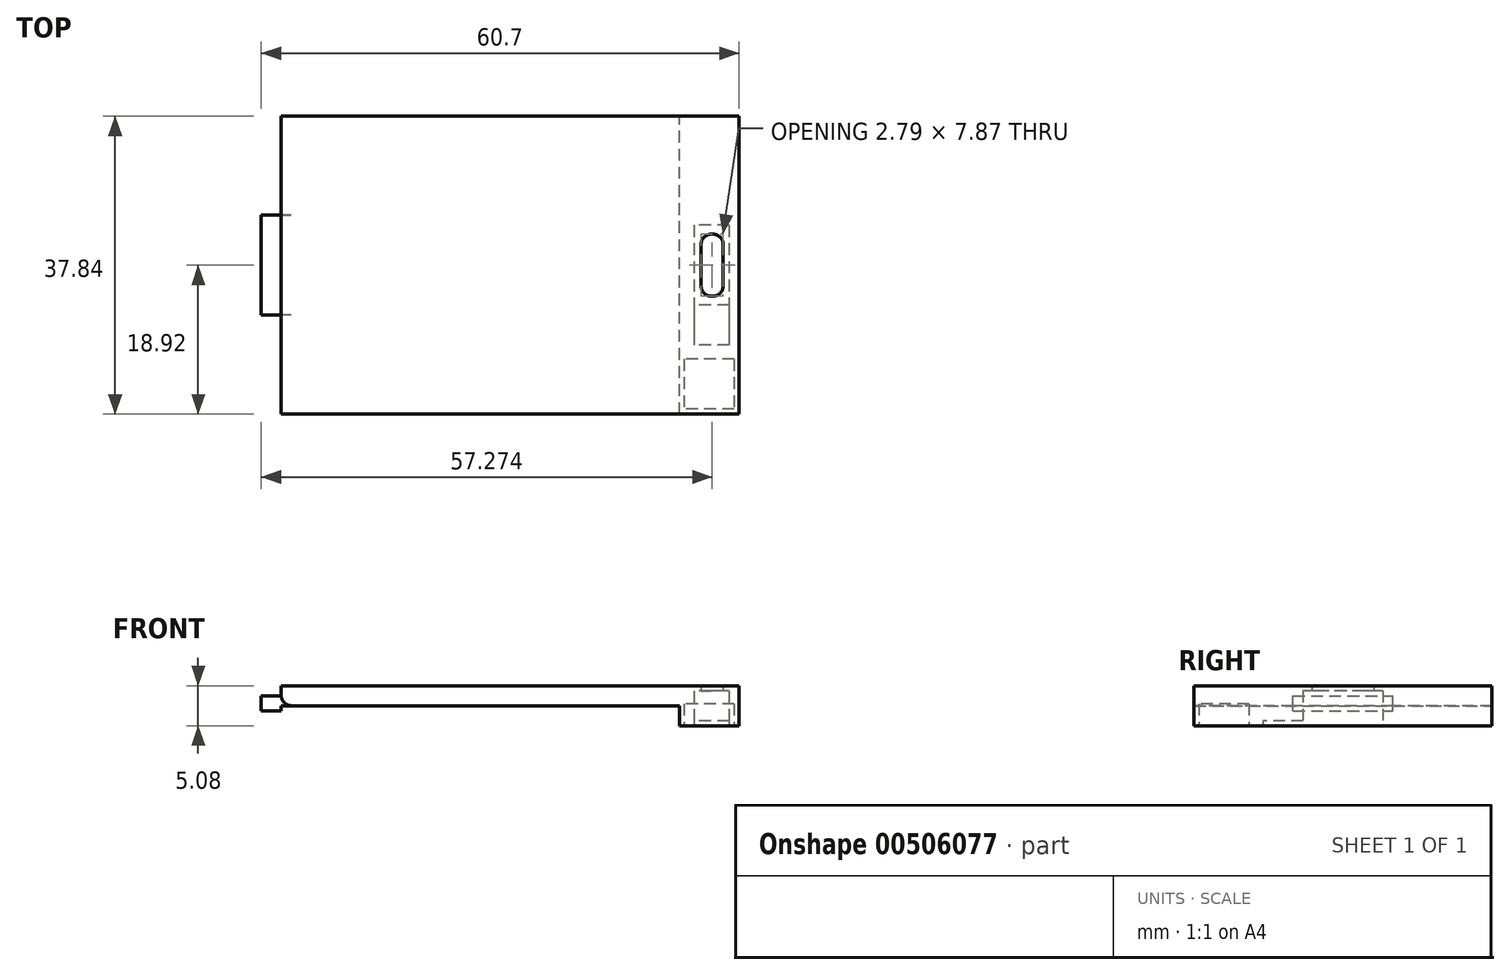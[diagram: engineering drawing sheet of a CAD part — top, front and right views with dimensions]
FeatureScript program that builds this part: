
annotation { "Feature Type Name" : "Feature", "Feature Type Description" : "" }
export const myFeature = defineFeature(function(context is Context, id is Id, definition is map)
    precondition{}
    {
        {
            var Q0;
            Q0=qCreatedBy(makeId("Top.planeOp"),FACE);
            var sketch = newSketch(context, id + "F0", { "sketchPlane" : qUnion([Q0])});
            skLineSegment(sketch, "E0.bottom", {"start": v(29.08, 18.92) * mm, "end": v(-29.08, 18.92) * mm});
            skLineSegment(sketch, "E0.top", {"start": v(29.08, -18.92) * mm, "end": v(-29.08, -18.92) * mm});
            skLineSegment(sketch, "E0.left", {"start": v(29.08, 18.92) * mm, "end": v(29.08, -18.92) * mm});
            skLineSegment(sketch, "E0.right", {"start": v(-29.08, 18.92) * mm, "end": v(-29.08, -18.92) * mm});
            skPoint(sketch, "E0.middle", {"position": v(0, 0) * mm});
            skSolve(sketch);
        }
        {
            var Q0;
            Q0=makeQuery(id+"F0.imprint","IMPRINT",FACE,{"disambiguationData":[TD([[makeQuery(id+"F0.imprint","IMPRINT",EDGE,{"derivedFrom":sQuery(id+"F0.wireOp",EDGE,"E0.bottom")}),1.0]])]});
            extrude(context, id + "F1", {"entities" : qUnion([Q0]), "depth" : 2.54 * mm});
        }
        {
            var Q0;
            Q0=makeQuery(id+"F1.opExtrude","CAP_FACE",FACE,{"disambiguationData":[OSD([sQuery(id+"F0.wireOp",EDGE,"E0.bottom"),sQuery(id+"F0.wireOp",EDGE,"E0.top"),sQuery(id+"F0.wireOp",EDGE,"E0.left"),sQuery(id+"F0.wireOp",EDGE,"E0.right")])],"isStart":true});
            var sketch = newSketch(context, id + "F2", { "sketchPlane" : qUnion([Q0])});
            skLineSegment(sketch, "E1.bottom", {"start": v(29.08, 18.92) * mm, "end": v(21.49, 18.92) * mm});
            skLineSegment(sketch, "E1.top", {"start": v(29.08, -18.92) * mm, "end": v(21.49, -18.92) * mm});
            skLineSegment(sketch, "E1.left", {"start": v(29.08, 18.92) * mm, "end": v(29.08, -18.92) * mm});
            skLineSegment(sketch, "E1.right", {"start": v(21.49, 18.92) * mm, "end": v(21.49, -18.92) * mm});
            skSolve(sketch);
        }
        {
            var Q0;
            Q0=makeQuery(id+"F2.imprint","IMPRINT",FACE,{"disambiguationData":[TD([[makeQuery(id+"F2.imprint","IMPRINT",EDGE,{"derivedFrom":sQuery(id+"F2.wireOp",EDGE,"E1.bottom")}),1.0]])]});
            extrude(context, id + "F3", {"entities" : qUnion([Q0]), "operationType" : NewBodyOperationType.ADD, "depth" : 2.54 * mm});
        }
        {
            var Q0;
            Q0=makeQuery(id+"F1.opExtrude","SWEPT_FACE",FACE,{"disambiguationData":[OSD([sQuery(id+"F0.wireOp",EDGE,"E0.right")])]});
            var sketch = newSketch(context, id + "F4", { "sketchPlane" : qUnion([Q0])});
            skLineSegment(sketch, "E2.bottom", {"start": v(6.35, -0.63) * mm, "end": v(-6.35, -0.64) * mm});
            skLineSegment(sketch, "E2.top", {"start": v(6.35, 1.27) * mm, "end": v(-6.35, 1.27) * mm});
            skLineSegment(sketch, "E2.left", {"start": v(6.35, -0.63) * mm, "end": v(6.35, 1.27) * mm});
            skLineSegment(sketch, "E2.right", {"start": v(-6.35, -0.64) * mm, "end": v(-6.35, 1.27) * mm});
            skPoint(sketch, "E2.middle", {"position": v(0, 0.32) * mm});
            skSolve(sketch);
        }
        {
            var Q0;
            {var subQ0=sQuery(id+"F4.wireOp",EDGE,"E2.bottom");Q0=makeQuery(id+"F4.imprint","IMPRINT",FACE,{"disambiguationData":[TD([[makeQuery(id+"F4.imprint","IMPRINT",EDGE,{"derivedFrom":subQ0}),-1.0]])]});}
            var Q1;
            {var subQ0=sQuery(id+"F4.wireOp",EDGE,"E2.top");Q1=makeQuery(id+"F4.imprint","IMPRINT",FACE,{"disambiguationData":[TD([[makeQuery(id+"F4.imprint","IMPRINT",EDGE,{"derivedFrom":subQ0}),1.0]])]});}
            extrude(context, id + "F5", {"entities" : qUnion([Q0, Q1]), "operationType" : NewBodyOperationType.ADD, "depth" : 2.54 * mm});
        }
        {
            var Q0;
            {var subQ0=sQuery(id+"F0.wireOp",EDGE,"E0.right");Q0=makeQuery(id+"F5.boolean.opBoolean","SPLIT",EDGE,{"disambiguationData":[topologyDisambiguationEdgeConnected([makeQuery(id+"F1.opExtrude","CAP_FACE",FACE,{"disambiguationData":[OSD([sQuery(id+"F0.wireOp",EDGE,"E0.bottom"),sQuery(id+"F0.wireOp",EDGE,"E0.top"),sQuery(id+"F0.wireOp",EDGE,"E0.left"),subQ0])],"isStart":true}),makeQuery(id+"F5.opExtrude","CAP_FACE",FACE,{"disambiguationData":[OSD([sQuery(id+"F4.wireOp",EDGE,"E2.bottom"),sQuery(id+"F4.wireOp",EDGE,"E2.top"),sQuery(id+"F4.wireOp",EDGE,"E2.left"),sQuery(id+"F4.wireOp",EDGE,"E2.right")])],"isStart":true})])],"derivedFrom":makeQuery(id+"F1.opExtrude","CAP_EDGE",EDGE,{"disambiguationData":[OSD([subQ0])],"isStart":true})});}
            fillet(context, id + "F6", {"entities" : qUnion([Q0]), "radius" : 1.27 * mm, "tangentPropagation" : true, "allowEdgeOverflow" : false});
        }
        {
            var Q0;
            Q0=makeQuery(id+"F3.opExtrude","CAP_FACE",FACE,{"disambiguationData":[OSD([sQuery(id+"F2.wireOp",EDGE,"E1.bottom"),sQuery(id+"F2.wireOp",EDGE,"E1.top"),sQuery(id+"F2.wireOp",EDGE,"E1.left"),sQuery(id+"F2.wireOp",EDGE,"E1.right")])],"isStart":false});
            var sketch = newSketch(context, id + "F7", { "sketchPlane" : qUnion([Q0])});
            skLineSegment(sketch, "E3.bottom", {"start": v(27.81, -5.08) * mm, "end": v(23.37, -5.08) * mm});
            skLineSegment(sketch, "E3.top", {"start": v(27.81, 5.08) * mm, "end": v(23.37, 5.08) * mm});
            skLineSegment(sketch, "E3.left", {"start": v(27.81, -5.08) * mm, "end": v(27.81, 5.08) * mm});
            skLineSegment(sketch, "E3.right", {"start": v(23.37, -5.08) * mm, "end": v(23.37, 5.08) * mm});
            skPoint(sketch, "E3.middle", {"position": v(25.6, 0) * mm});
            skPoint(sketch, "E4", {"position": v(21.49, 0) * mm});
            skSolve(sketch);
        }
        {
            var Q0;
            Q0=makeQuery(id+"F7.imprint","IMPRINT",FACE,{"disambiguationData":[TD([[makeQuery(id+"F7.imprint","IMPRINT",EDGE,{"derivedFrom":sQuery(id+"F7.wireOp",EDGE,"E3.bottom")}),-1.0]])]});
            extrude(context, id + "F8", {"entities" : qUnion([Q0]), "operationType" : NewBodyOperationType.REMOVE, "oppositeDirection" : true, "depth" : 4.44 * mm});
        }
        {
            var Q0;
            Q0=makeQuery(id+"F3.opExtrude","CAP_FACE",FACE,{"disambiguationData":[OSD([sQuery(id+"F2.wireOp",EDGE,"E1.bottom"),sQuery(id+"F2.wireOp",EDGE,"E1.top"),sQuery(id+"F2.wireOp",EDGE,"E1.left"),sQuery(id+"F2.wireOp",EDGE,"E1.right")])],"isStart":false});
            var sketch = newSketch(context, id + "F9", { "sketchPlane" : qUnion([Q0])});
            skLineSegment(sketch, "E5.bottom", {"start": v(27.81, 5.08) * mm, "end": v(23.37, 5.08) * mm});
            skLineSegment(sketch, "E5.top", {"start": v(27.81, 10.16) * mm, "end": v(23.37, 10.16) * mm});
            skLineSegment(sketch, "E5.left", {"start": v(27.81, 5.08) * mm, "end": v(27.81, 10.16) * mm});
            skLineSegment(sketch, "E5.right", {"start": v(23.37, 5.08) * mm, "end": v(23.37, 10.16) * mm});
            skSolve(sketch);
        }
        {
            var Q0;
            Q0=makeQuery(id+"F9.imprint","IMPRINT",FACE,{"disambiguationData":[TD([[makeQuery(id+"F9.imprint","IMPRINT",EDGE,{"derivedFrom":sQuery(id+"F9.wireOp",EDGE,"E5.bottom")}),-1.0]])]});
            extrude(context, id + "F10", {"entities" : qUnion([Q0]), "operationType" : NewBodyOperationType.REMOVE, "oppositeDirection" : true, "depth" : 0.64 * mm});
        }
        {
            var Q0;
            Q0=makeQuery(id+"F8.boolean.opBoolean","COPY",FACE,{"derivedFrom":makeQuery(id+"F8.opExtrude","CAP_FACE",FACE,{"disambiguationData":[OSD([sQuery(id+"F7.wireOp",EDGE,"E3.bottom"),sQuery(id+"F7.wireOp",EDGE,"E3.top"),sQuery(id+"F7.wireOp",EDGE,"E3.left"),sQuery(id+"F7.wireOp",EDGE,"E3.right")])],"isStart":false})});
            var sketch = newSketch(context, id + "F11", { "sketchPlane" : qUnion([Q0])});
            skLineSegment(sketch, "E6.bottom", {"start": v(25.78, -3.94) * mm, "end": v(25.53, -3.94) * mm});
            skLineSegment(sketch, "E6.top", {"start": v(25.78, 3.94) * mm, "end": v(25.53, 3.94) * mm});
            skLineSegment(sketch, "E6.left", {"start": v(27.05, -2.67) * mm, "end": v(27.05, 2.67) * mm});
            skLineSegment(sketch, "E6.right", {"start": v(24.26, -2.67) * mm, "end": v(24.26, 2.67) * mm});
            skPoint(sketch, "E6.middle", {"position": v(25.65, 0) * mm});
            skPoint(sketch, "E6.middle.positionSnap0", {"position": v(27.81, 0) * mm});
            skPoint(sketch, "E6.centerSnap0", {"position": v(27.81, 0) * mm});
            skPoint(sketch, "E7.visualSharp", {"position": v(27.05, 3.94) * mm});
            skArc(sketch, "E7.filletArc", {"start": v(27.05, 2.67) * mm, "mid": v(26.68, 3.57) * mm, "end": v(25.78, 3.94) * mm});
            skPoint(sketch, "E8.visualSharp", {"position": v(24.26, 3.94) * mm});
            skArc(sketch, "E8.filletArc", {"start": v(25.53, 3.94) * mm, "mid": v(24.63, 3.57) * mm, "end": v(24.26, 2.67) * mm});
            skPoint(sketch, "E9.visualSharp", {"position": v(24.26, -3.94) * mm});
            skArc(sketch, "E9.filletArc", {"start": v(24.26, -2.67) * mm, "mid": v(24.63, -3.57) * mm, "end": v(25.53, -3.94) * mm});
            skPoint(sketch, "E10.visualSharp", {"position": v(27.05, -3.94) * mm});
            skArc(sketch, "E10.filletArc", {"start": v(25.78, -3.94) * mm, "mid": v(26.68, -3.57) * mm, "end": v(27.05, -2.67) * mm});
            skSolve(sketch);
        }
        {
            var Q0;
            Q0=makeQuery(id+"F11.imprint","IMPRINT",FACE,{"disambiguationData":[TD([[makeQuery(id+"F11.imprint","IMPRINT",EDGE,{"derivedFrom":sQuery(id+"F11.wireOp",EDGE,"E6.bottom")}),-1.0]])]});
            extrude(context, id + "F12", {"entities" : qUnion([Q0]), "operationType" : NewBodyOperationType.REMOVE, "endBound" : BoundingType.UP_TO_NEXT, "oppositeDirection" : true, "depth" : 25.4 * mm});
        }
        {
            var Q0;
            Q0=makeQuery(id+"F3.opExtrude","CAP_FACE",FACE,{"disambiguationData":[OSD([sQuery(id+"F2.wireOp",EDGE,"E1.bottom"),sQuery(id+"F2.wireOp",EDGE,"E1.top"),sQuery(id+"F2.wireOp",EDGE,"E1.left"),sQuery(id+"F2.wireOp",EDGE,"E1.right")])],"isStart":false});
            var sketch = newSketch(context, id + "F13", { "sketchPlane" : qUnion([Q0])});
            skLineSegment(sketch, "E11.bottom", {"start": v(28.45, 11.94) * mm, "end": v(22.1, 11.94) * mm});
            skLineSegment(sketch, "E11.top", {"start": v(28.45, 18.29) * mm, "end": v(22.1, 18.29) * mm});
            skLineSegment(sketch, "E11.left", {"start": v(28.45, 11.94) * mm, "end": v(28.45, 18.29) * mm});
            skLineSegment(sketch, "E11.right", {"start": v(22.1, 11.94) * mm, "end": v(22.1, 18.29) * mm});
            skPoint(sketch, "E11.middle", {"position": v(25.27, 15.11) * mm});
            skSolve(sketch);
        }
        {
            var Q0;
            Q0=makeQuery(id+"F13.imprint","IMPRINT",FACE,{"disambiguationData":[TD([[makeQuery(id+"F13.imprint","IMPRINT",EDGE,{"derivedFrom":sQuery(id+"F13.wireOp",EDGE,"E11.bottom")}),-1.0]])]});
            extrude(context, id + "F14", {"entities" : qUnion([Q0]), "operationType" : NewBodyOperationType.REMOVE, "oppositeDirection" : true, "depth" : 2.8 * mm});
        }
    });
